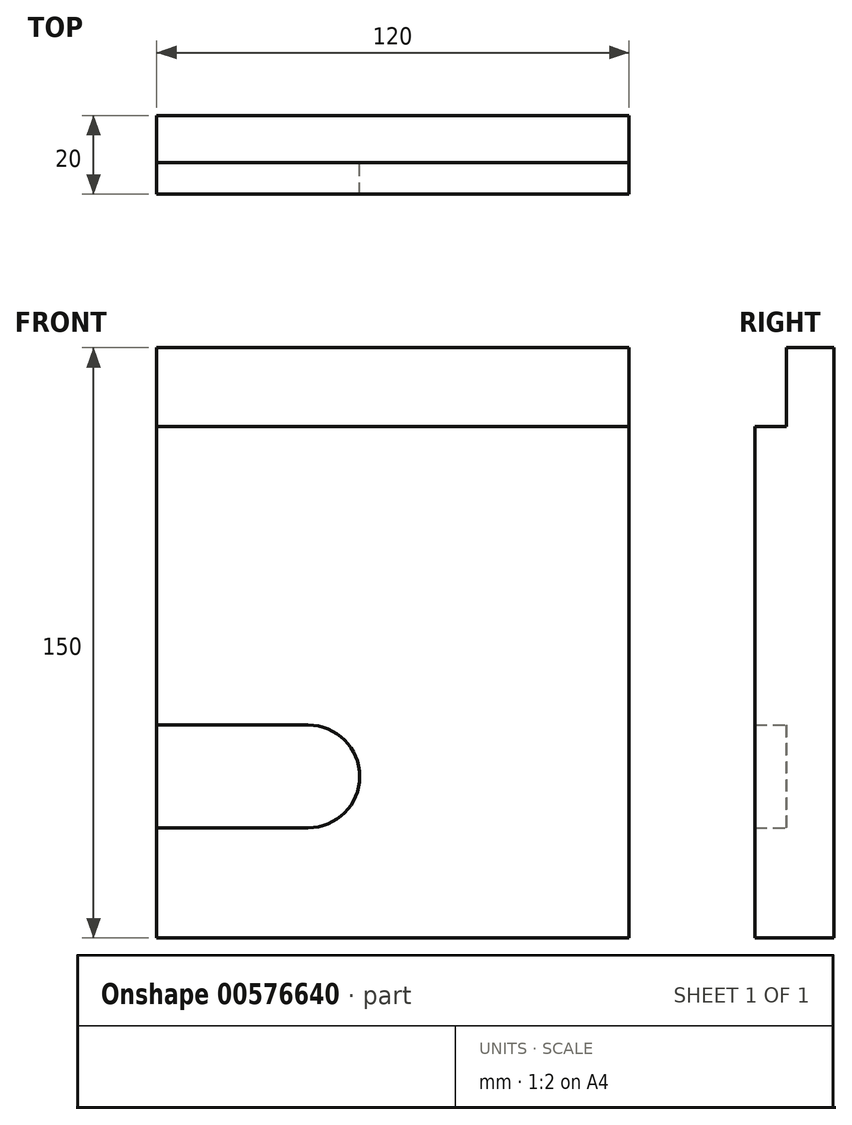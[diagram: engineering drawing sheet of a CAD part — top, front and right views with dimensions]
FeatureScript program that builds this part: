
annotation { "Feature Type Name" : "Feature", "Feature Type Description" : "" }
export const myFeature = defineFeature(function(context is Context, id is Id, definition is map)
    precondition{}
    {
        {
            var Q0;
            Q0=qCreatedBy(makeId("Front.planeOp"),FACE);
            var sketch = newSketch(context, id + "F0", { "sketchPlane" : qUnion([Q0])});
            skLineSegment(sketch, "E0", {"start": v(-120, 95.88) * mm, "end": v(-120, -54.12) * mm});
            skLineSegment(sketch, "E1", {"start": v(-120, -54.12) * mm, "end": v(0, -54.12) * mm});
            skLineSegment(sketch, "E2", {"start": v(0, -54.12) * mm, "end": v(0, -26.12) * mm});
            skLineSegment(sketch, "E3", {"start": v(0, -26.12) * mm, "end": v(0, -1.12) * mm});
            skLineSegment(sketch, "E4", {"start": v(-120, 95.88) * mm, "end": v(0, 95.88) * mm});
            skLineSegment(sketch, "E5", {"start": v(-120, 75.88) * mm, "end": v(0, 75.88) * mm});
            skLineSegment(sketch, "E6", {"start": v(0, -1.12) * mm, "end": v(0, 75.88) * mm});
            skLineSegment(sketch, "E7", {"start": v(0, 75.88) * mm, "end": v(0, 95.88) * mm});
            skLineSegment(sketch, "E8", {"start": v(0, 0) * mm, "end": v(-81.5, 0) * mm});
            skLineSegment(sketch, "E9", {"start": v(-81.5, 0) * mm, "end": v(-120, 0) * mm});
            skLineSegment(sketch, "E10", {"start": v(0, -26.12) * mm, "end": v(-81.5, -26.12) * mm});
            skLineSegment(sketch, "E11", {"start": v(-81.5, -26.12) * mm, "end": v(-120, -26.12) * mm});
            skArc(sketch, "E12", {"start": v(-81.5, -26.12) * mm, "mid": v(-68.44, -13.06) * mm, "end": v(-81.5, 0) * mm});
            skSolve(sketch);
        }
        {
            var Q0;
            {var subQ0=sQuery(id+"F0.wireOp",EDGE,"E4");Q0=makeQuery(id+"F0.imprint","IMPRINT",FACE,{"disambiguationData":[TD([[makeQuery(id+"F0.imprint","IMPRINT",EDGE,{"derivedFrom":subQ0}),-1.0]])]});}
            extrude(context, id + "F1", {"entities" : qUnion([Q0]), "depth" : 12 * mm, "offsetDistance" : 25 * mm});
        }
        {
            var Q0;
            {var subQ1=sQuery(id+"F0.wireOp",EDGE,"E5");Q0=makeQuery(id+"F0.imprint","IMPRINT",FACE,{"disambiguationData":[TD([[makeQuery(id+"F0.imprint","IMPRINT",EDGE,{"derivedFrom":subQ1}),-1.0]])]});}
            extrude(context, id + "F2", {"entities" : qUnion([Q0]), "operationType" : NewBodyOperationType.ADD, "depth" : 20 * mm, "offsetDistance" : 25 * mm});
        }
        {
            var Q0;
            {var subQ2=sQuery(id+"F0.wireOp",EDGE,"E3");Q0=makeQuery(id+"F0.imprint","IMPRINT",FACE,{"disambiguationData":[TD([[makeQuery(id+"F0.imprint","IMPRINT",EDGE,{"derivedFrom":subQ2}),1.0]])]});}
            extrude(context, id + "F3", {"entities" : qUnion([Q0]), "operationType" : NewBodyOperationType.ADD, "depth" : 20 * mm, "offsetDistance" : 25 * mm});
        }
        {
            var Q0;
            {var subQ0=sQuery(id+"F0.wireOp",EDGE,"E1");Q0=makeQuery(id+"F0.imprint","IMPRINT",FACE,{"disambiguationData":[TD([[makeQuery(id+"F0.imprint","IMPRINT",EDGE,{"derivedFrom":subQ0}),1.0]])]});}
            extrude(context, id + "F4", {"entities" : qUnion([Q0]), "operationType" : NewBodyOperationType.ADD, "depth" : 20 * mm, "offsetDistance" : 25 * mm});
        }
        {
            var Q0;
            {var subQ0=sQuery(id+"F0.wireOp",EDGE,"E9");Q0=makeQuery(id+"F0.imprint","IMPRINT",FACE,{"disambiguationData":[TD([[makeQuery(id+"F0.imprint","IMPRINT",EDGE,{"derivedFrom":subQ0}),1.0]])]});}
            extrude(context, id + "F5", {"entities" : qUnion([Q0]), "operationType" : NewBodyOperationType.ADD, "depth" : 12 * mm, "offsetDistance" : 25 * mm});
        }
    });
